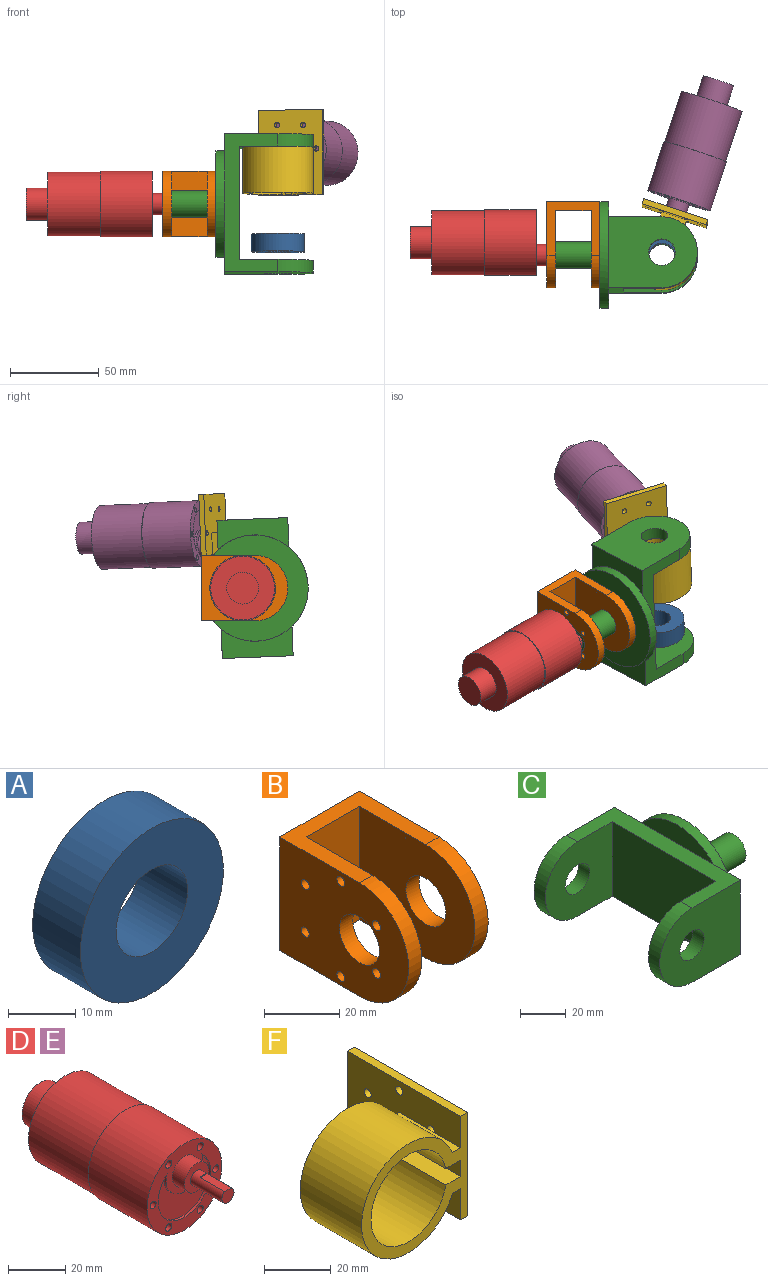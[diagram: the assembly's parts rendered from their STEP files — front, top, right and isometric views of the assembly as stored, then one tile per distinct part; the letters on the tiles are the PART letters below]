
ASSEMBLY  parts=6 mates=8
PART A: 4 faces, bbox 30x10x30 mm
  f0: cylinder r=7.5mm len=15mm, axis (0,1,0), area 471.2mm2, adj f2,f3
  f1: cylinder r=15mm len=30mm, axis (0,1,0), area 942.5mm2, adj f2,f3
  f2: plane 30x30mm, normal (0,-1,0), area 530.1mm2, adj f0,f1
  f3: plane 30x30mm, normal (0,1,0), area 530.1mm2, adj f0,f1
PART B: 22 faces, bbox 30x48.5x37 mm
  f0: plane 48.5x37mm, normal (-1,0,0), area 1428.5mm2, adj f1,f2,f4,f5,f7,f12,f17,f18
  f1: cylinder r=1.5mm len=5mm, axis (-1,0,0), area 47.1mm2, adj f0,f13
  f2: cylinder r=1.5mm len=5mm, axis (-1,0,0), area 47.1mm2, adj f0,f13
  f3: cylinder r=18.5mm len=37mm, axis (-1,0,0), area 290.6mm2, adj f4,f5,f6,f14
  f4: plane 30x30mm, normal (0,0,1), area 400mm2, adj f0,f3,f6,f7,f12,f13,f14,f15
  f5: plane 30x30mm, normal (0,0,-1), area 400mm2, adj f0,f3,f6,f7,f12,f13,f14,f15
  f6: plane 48.5x37mm, normal (1,0,0), area 1470.9mm2, adj f3,f4,f5,f7,f8,f9,f10,f11
  f7: plane 37x30mm, normal (0,1,0), area 1110mm2, adj f0,f4,f5,f6
  f8: cylinder r=1.5mm len=5mm, axis (-1,0,0), area 1.5mm2, adj f6,f9,f14
  f9: cylinder r=18.5mm len=5mm, axis (-1,0,0), area 1.5mm2, adj f6,f8,f14
  f10: cylinder r=1.5mm len=5mm, axis (-1,0,0), area 1.5mm2, adj f6,f11,f14
  f11: cylinder r=18.5mm len=5mm, axis (-1,0,0), area 1.5mm2, adj f6,f10,f14
  f12: cylinder r=18.5mm len=37mm, axis (-1,0,0), area 290.6mm2, adj f0,f4,f5,f13
  f13: plane 43.5x37mm, normal (1,0,0), area 1243.5mm2, adj f1,f2,f4,f5,f12,f15,f17,f18
  f14: plane 43.5x37mm, normal (-1,0,0), area 1285.9mm2, adj f3,f4,f5,f8,f9,f10,f11,f15
  f15: plane 37x20mm, normal (0,-1,0), area 740mm2, adj f4,f5,f13,f14
  f16: cylinder r=7.5mm len=15mm, axis (-1,0,0), area 235.6mm2, adj f6,f14
  f17: cylinder r=7.5mm len=15mm, axis (-1,0,0), area 235.6mm2, adj f0,f13
  f18: cylinder r=1.5mm len=5mm, axis (-1,0,0), area 47.1mm2, adj f0,f13
  f19: cylinder r=1.5mm len=5mm, axis (-1,0,0), area 47.1mm2, adj f0,f13
  f20: cylinder r=1.5mm len=5mm, axis (-1,0,0), area 47.1mm2, adj f0,f13
  f21: cylinder r=1.5mm len=5mm, axis (-1,0,0), area 47.1mm2, adj f0,f13
PART C: 21 faces, bbox 85x78x60 mm
  f0: cylinder r=20mm len=40mm, axis (0,1,0), area 439.8mm2, adj f1,f2,f15,f16
  f1: plane 78x30mm, normal (0,0,-1), area 967mm2, adj f0,f10,f11,f12,f13,f14,f15,f16
  f2: plane 78x30mm, normal (0,0,1), area 967mm2, adj f0,f3,f11,f12,f13,f14,f15,f16
  f3: plane 44.72x10mm, normal (-1,0,0), area 309.7mm2, adj f2,f9
  f4: plane 6x6mm, normal (1,0,0), area 28.3mm2, adj f5
  f5: cylinder r=3mm len=16mm, axis (-1,0,0), area 301.6mm2, adj f4,f6
  f6: plane 15x15mm, normal (1,0,0), area 148.4mm2, adj f5,f7
  f7: cylinder r=7.5mm len=30mm, axis (-1,0,0), area 1413.7mm2, adj f6,f8
  f8: plane 60x60mm, normal (1,0,0), area 2650.7mm2, adj f7,f9
  f9: cylinder r=30mm len=60mm, axis (-1,0,0), area 942.5mm2, adj f3,f8,f10,f11,f13
  f10: plane 44.72x10mm, normal (-1,0,0), area 309.7mm2, adj f1,f9
  f11: plane 40x16.64mm, normal (1,0,0), area 456mm2, adj f1,f2,f9,f15
  f12: cylinder r=20mm len=40mm, axis (0,1,0), area 439.8mm2, adj f1,f2,f14,f17
  f13: plane 40x16.64mm, normal (1,0,0), area 456mm2, adj f1,f2,f9,f14
  f14: plane 50x40mm, normal (0,-1,0), area 1651.6mm2, adj f1,f2,f12,f13,f19
  f15: plane 50x40mm, normal (0,1,0), area 1651.6mm2, adj f0,f1,f2,f11,f20
  f16: plane 41.45x40mm, normal (0,-1,0), area 1309.8mm2, adj f0,f1,f2,f18,f20
  f17: plane 41.45x40mm, normal (0,1,0), area 1309.8mm2, adj f1,f2,f12,f18,f19
  f18: plane 64x40mm, normal (-1,0,0), area 2560mm2, adj f1,f2,f16,f17
  f19: cylinder r=7.5mm len=15mm, axis (0,-1,0), area 329.9mm2, adj f14,f17
  f20: cylinder r=7.5mm len=15mm, axis (0,-1,0), area 329.9mm2, adj f15,f16
PART D: 28 faces, bbox 37x92.7x37 mm
  f0: plane 37x37mm, normal (0,-1,0), area 603mm2, adj f1,f7,f11,f13,f15,f17,f19,f21
  f1: cylinder r=18.5mm len=37mm, axis (0,-1,0), area 3370.9mm2, adj f0,f2
  f2: plane 37x37mm, normal (0,1,0), area 57.3mm2, adj f1,f3
  f3: cylinder r=18mm len=36mm, axis (0,-1,0), area 3392.9mm2, adj f2,f4
  f4: plane 36x36mm, normal (0,1,0), area 763.4mm2, adj f3,f5
  f5: cylinder r=9mm len=18mm, axis (0,-1,0), area 692.2mm2, adj f4,f6
  f6: plane 18x18mm, normal (0,1,0), area 254.5mm2, adj f5
  f7: cylinder r=6mm len=12mm, axis (0,1,0), area 226.2mm2, adj f0,f8
  f8: plane 12x12mm, normal (0,-1,0), area 84.8mm2, adj f7,f9
  f9: cylinder r=3mm len=15.5mm, axis (0,1,0), area 250mm2, adj f8,f10,f23,f24
  f10: plane 6x5.5mm, normal (0,-1,0), area 27.1mm2, adj f9,f24
  f11: cylinder r=1.5mm len=10mm, axis (0,-1,0), area 94.2mm2, adj f0,f12
  f12: plane 3x3mm, normal (0,-1,0), area 7.1mm2, adj f11
  f13: cylinder r=1.5mm len=10mm, axis (0,-1,0), area 94.2mm2, adj f0,f14
  f14: plane 3x3mm, normal (0,-1,0), area 7.1mm2, adj f13
  f15: cylinder r=1.5mm len=10mm, axis (0,-1,0), area 94.2mm2, adj f0,f16
  f16: plane 3x3mm, normal (0,-1,0), area 7.1mm2, adj f15
  f17: cylinder r=1.5mm len=10mm, axis (0,-1,0), area 94.2mm2, adj f0,f18
  f18: plane 3x3mm, normal (0,-1,0), area 7.1mm2, adj f17
  f19: cylinder r=1.5mm len=10mm, axis (0,-1,0), area 94.2mm2, adj f0,f20
  f20: plane 3x3mm, normal (0,-1,0), area 7.1mm2, adj f19
  f21: cylinder r=1.5mm len=10mm, axis (0,-1,0), area 94.2mm2, adj f0,f22
  f22: plane 3x3mm, normal (0,-1,0), area 7.1mm2, adj f21
  f23: plane 3.32x0.5mm, normal (0,-1,0), area 1.1mm2, adj f9,f24
  f24: plane 12x3.32mm, normal (0,0,1), area 39.8mm2, adj f9,f10,f23
  f25: cylinder r=13mm len=26mm, axis (0,-1,0), area 63mm2, adj f0,f26,f27
  f26: cylinder r=9mm len=18mm, axis (0,-1,0), area 33.9mm2, adj f0,f25,f27
  f27: plane 26x22.79mm, normal (0,-1,0), area 316.7mm2, adj f25,f26
PART E: same geometry as D
PART F: 26 faces, bbox 45x48x40 mm
  f0: plane 48x38mm, normal (-1,0,0), area 1397.2mm2, adj f1,f2,f3,f8,f12,f14,f15,f16
  f1: plane 26x3.46mm, normal (0,0,1), area 89.9mm2, adj f0,f3,f7,f8,f23
  f2: plane 26x3.46mm, normal (0,0,-1), area 89.9mm2, adj f0,f3,f7,f8,f22
  f3: plane 42x40mm, normal (0,1,0), area 1117.1mm2, adj f0,f1,f2,f7,f25
  f4: plane 23x6.28mm, normal (0,0,-1), area 144.5mm2, adj f6,f8,f10,f11,f24
  f5: plane 23x6.28mm, normal (0,0,1), area 144.5mm2, adj f6,f8,f10,f11,f24
  f6: cylinder r=16mm len=32mm, axis (0,1,0), area 2173.4mm2, adj f4,f5,f8,f24
  f7: cylinder r=20mm len=40mm, axis (0,1,0), area 2867.5mm2, adj f1,f2,f3,f8
  f8: plane 45x40mm, normal (0,-1,0), area 567mm2, adj f0,f1,f2,f4,f5,f6,f7,f9
  f9: plane 48x38mm, normal (1,0,0), area 1753.3mm2, adj f8,f12,f13,f14,f15,f16,f17,f18
  f10: plane 19x6mm, normal (-1,0,0), area 99.9mm2, adj f4,f5,f8,f13
  f11: plane 6x4mm, normal (-1,0,0), area 9.9mm2, adj f4,f5,f13,f24
  f12: cylinder r=1.5mm len=3mm, axis (1,0,0), area 28.3mm2, adj f0,f9,f22
  f13: cylinder r=3mm len=6mm, axis (1,0,0), area 56.5mm2, adj f9,f10,f11
  f14: plane 48x3mm, normal (0,0,-1), area 144mm2, adj f0,f8,f9,f15
  f15: plane 38x3mm, normal (0,1,0), area 114mm2, adj f0,f9,f14,f19
  f16: cylinder r=1.5mm len=3mm, axis (1,0,0), area 28.3mm2, adj f0,f9
  f17: cylinder r=1.5mm len=3mm, axis (1,0,0), area 28.3mm2, adj f0,f9
  f18: cylinder r=1.5mm len=3mm, axis (1,0,0), area 28.3mm2, adj f0,f9
  f19: plane 48x3mm, normal (0,0,1), area 144mm2, adj f0,f8,f9,f15
  f20: cylinder r=1.5mm len=3mm, axis (1,0,0), area 28.3mm2, adj f0,f9
  f21: cylinder r=1.5mm len=3mm, axis (1,0,0), area 28.3mm2, adj f0,f9,f23
  f22: plane 2.96x1.25mm, normal (1,0,0), area 2.8mm2, adj f2,f12
  f23: plane 2.96x1.25mm, normal (1,0,0), area 2.8mm2, adj f1,f21
  f24: plane 38x32mm, normal (0,-1,0), area 664.1mm2, adj f4,f5,f6,f11,f25
  f25: cylinder r=7.5mm len=15mm, axis (0,1,0), area 141.4mm2, adj f3,f24
PLACE A rot(axis=(0.52,0.62,0.59),123.4deg) t=(55.91,-6.81,-22.7)mm
PLACE B t=(-9.09,18.85,-24.22)mm fixed
PLACE C rot(axis=(0,-0.69,0.72),180deg) t=(25.91,-6.15,-5.72)mm
PLACE D rot(axis=(0.58,-0.58,0.58),120deg) t=(-15.09,0.85,-5.72)mm
PLACE E rot(axis=(0.16,0.99,-0.02),179.6deg) t=(65.59,24.53,25.11)mm
PLACE F rot(axis=(0.69,0.52,0.5),108.6deg) t=(55.91,-4.9,26.26)mm
MATE revolute C.f5 <-> B.f3  axis (-1,0,0) through (20.91,-6.15,-5.72)mm
MATE cylindrical B.f21 <-> D.f21  axis (-1,0,0) through (-9.09,-12.57,2.03)mm
MATE revolute F.f6 <-> C.f19  axis (0,0.04,1) through (55.91,-4.9,26.26)mm
MATE planar C.f16 <-> A.f1  axis (0,0.04,1) through (52.96,-7.4,-37.69)mm
MATE cylindrical F.f21 <-> E.f11  axis (0.31,0.95,-0.04) through (70.61,14.47,12.07)mm
MATE revolute E.f7 <-> F.f13  axis (-0.31,-0.95,0.04) through (63.71,18.56,18.34)mm
MATE cylindrical A.f0 <-> C.f19  axis (0,0.04,1) through (55.91,-6.81,-22.7)mm
MATE revolute D.f7 <-> C.f5  axis (1,0,0) through (-9.09,-6.15,-5.72)mm
